# Revit family: FLX_Spotlight_Skin+Bones_Ceiling Hosted
name_source: partatom
category: Lighting Fixtures
revit_build: Autodesk Revit 2018 (Build: 20180423_1000(x64)
units: mm (PartAtom-declared; Revit-internal decimal feet)

## family parameters
Always vertical = Yes
Cut with Voids When Loaded = No
Host = Ceiling
Light Source = Yes
OmniClass Number = 23.80.70.11
OmniClass Title = Luminaries for Internal Lighting
Part Type = Normal
Room Calculation Point = No
Round Connector Dimension = Use Diameter
Shared = No

## types (4) — shared parameters
21deg Soft Beam = No
2700K = No
3000K = No
3500K = No
38deg Soft Beam = No
4000K = No
59deg Soft Beam = No
Analogue 1-10V = No
Casambi = No
Color Filter = 16777215
DALI = No
Description = Skin+Bones™ Spotlight
Detail = FLX_Finish_Black
Dimming Lamp Color Temperature Shift = <None>
Emit Shape Visible in Rendering = No
Emit from Circle Diameter = 70 mm  [stored 0.229659 ft]
Finish = FLX_Finish_Stone Rumbled Aluminium
Honeycomb Louvre = No
Manufacturer = Factorylux®
Model = Please Select 01 Option For Each Configuration Category in The Family Type Properties
No Accessory = Yes
Spreader Lens = No
Stone Rumbled Aluminium = Yes
Tilt Angle = 90.00°
Type Comments = Please use the Type Catalog to get the correct photometric. This is a generic family type and the photometric representation may not correspond to your specification.
URL = https://factorylux.com
Uniclass2015Code = Pr_70_70_48_82
Uniclass2015Title = Spotlights
Uniclass2015Version = Products v1.31
Wall Wash = No

## per-type parameters (varying)
| type | Control Additional Support Position | Control Additional Support Visibility | Control Light Source Alignment | Control Tilt Angle Center Position | Disc Monopoint | Large Monopoint | Small Monopoint | Spotlight Ceiling Offset | Support Height | Track Adapter | Type Image |
| _Generic_Large Monopoint, Stone Rumbled Aluminium | 75 mm | Yes | 295.5 mm | 145.5 mm  [stored 0.477362 ft] | No | Yes | No | 217 mm  [stored 0.711942 ft] | 105.5 mm  [stored 0.346129 ft] | No | SkinAndBones_Spotlight_2023_Track.png (2) |
| _Generic_Disc Monopoint, Stone Rumbled Aluminium | 2 mm  [stored 0.00656168 ft] | Yes | 221.5 mm  [stored 0.726706 ft] | 71.5 mm | Yes | No | No | 143 mm | 32.5 mm  [stored 0.106627 ft] | No | SkinAndBones_Spotlight_2023_Disc-1.png (2) |
| _Generic_Small Monopoint, Stone Rumbled Aluminium | 30 mm  [stored 0.0984252 ft] | Yes | 250.5 mm  [stored 0.82185 ft] | 100.5 mm  [stored 0.329724 ft] | No | No | Yes | 172 mm  [stored 0.564304 ft] | 60.5 mm  [stored 0.198491 ft] | No | SkinAndBones_Spotlight_2023_S-Mono.png (2) |
| _Generic_Track Adapter, Stone Rumbled Aluminium | 24.062 mm  [stored 0.0789436 ft] | No | 244.562 mm | 94.562 mm  [stored 0.310243 ft] | No | No | No | 166.4 mm  [stored 0.545932 ft] | 79.462 mm  [stored 0.260702 ft] | Yes | SkinAndBones_Spotlight_2023_S-Mono.png (2) |

note: [stored X ft] marks values corroborated as IEEE doubles in the binary element streams (Revit-internal decimal feet)

## geometry (parser evidence)
native form markers: Sweep x6
no freeform markers — native parametric forms only
